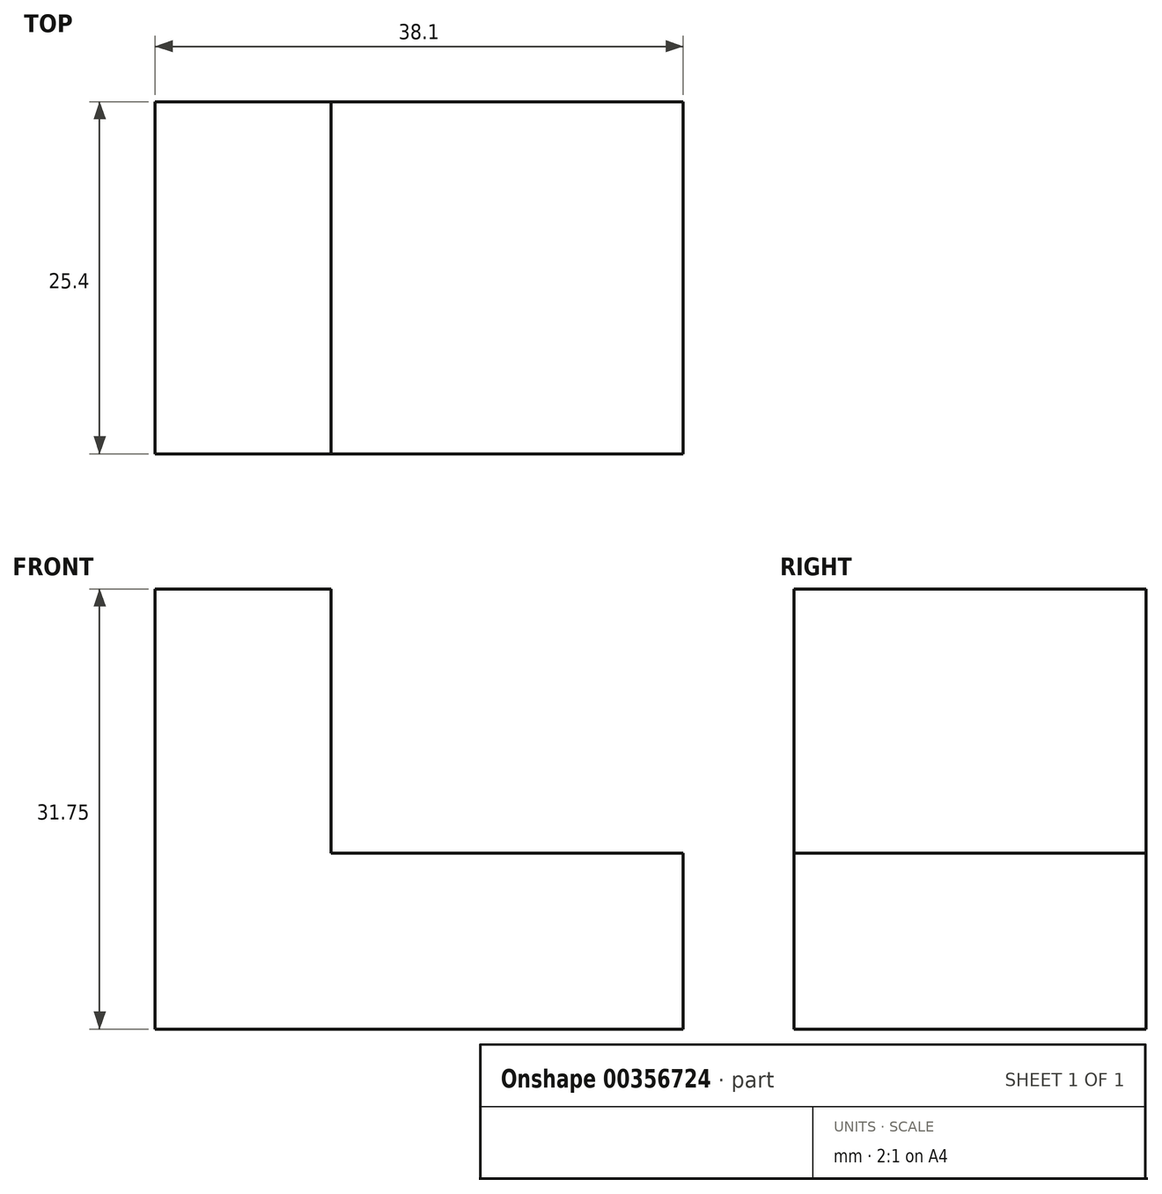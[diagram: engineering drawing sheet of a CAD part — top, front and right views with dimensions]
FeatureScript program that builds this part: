
annotation { "Feature Type Name" : "Feature", "Feature Type Description" : "" }
export const myFeature = defineFeature(function(context is Context, id is Id, definition is map)
    precondition{}
    {
        {
            var Q0;
            Q0=qCreatedBy(makeId("Front.planeOp"),FACE);
            var sketch = newSketch(context, id + "F0", { "sketchPlane" : qUnion([Q0])});
            skLineSegment(sketch, "E0", {"start": v(10.26, 0) * mm, "end": v(10.26, 31.75) * mm});
            skLineSegment(sketch, "E1", {"start": v(10.26, 31.75) * mm, "end": v(22.96, 31.75) * mm});
            skLineSegment(sketch, "E2", {"start": v(22.96, 31.75) * mm, "end": v(22.96, 12.7) * mm});
            skLineSegment(sketch, "E3", {"start": v(22.96, 12.7) * mm, "end": v(48.36, 12.7) * mm});
            skLineSegment(sketch, "E4", {"start": v(48.36, 12.7) * mm, "end": v(48.36, 0) * mm});
            skLineSegment(sketch, "E5", {"start": v(48.36, 0) * mm, "end": v(10.26, 0) * mm});
            skSolve(sketch);
        }
        {
            var Q0;
            Q0=makeQuery(id+"F0.imprint","IMPRINT",FACE,{"disambiguationData":[TD([[makeQuery(id+"F0.imprint","IMPRINT",EDGE,{"derivedFrom":sQuery(id+"F0.wireOp",EDGE,"E0")}),-1.0]])]});
            extrude(context, id + "F1", {"entities" : qUnion([Q0]), "depth" : 25.4 * mm});
        }
    });
